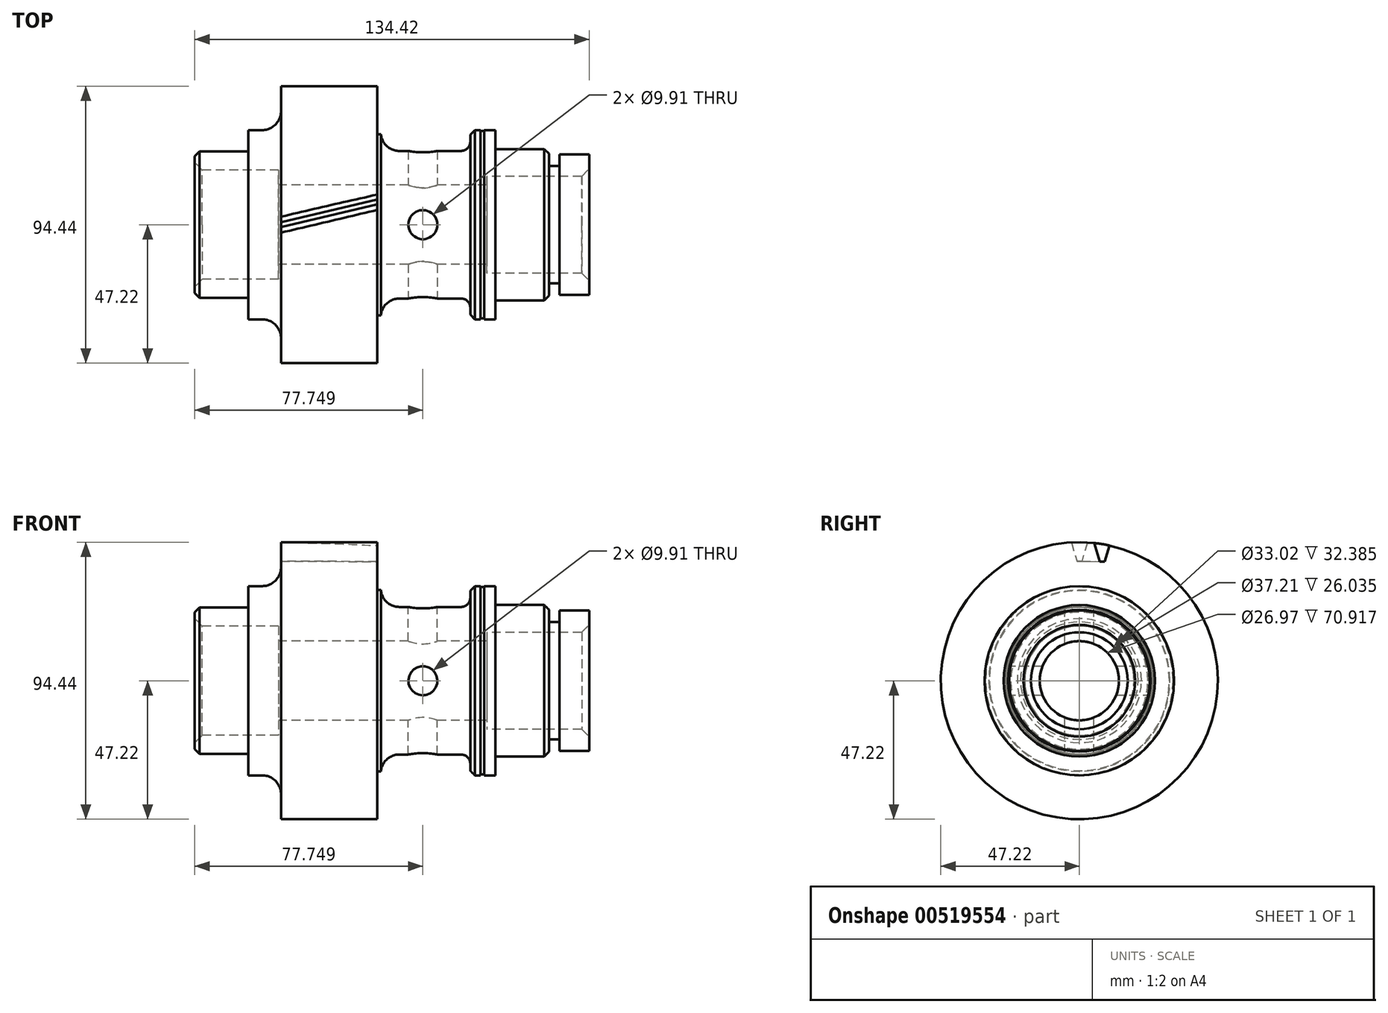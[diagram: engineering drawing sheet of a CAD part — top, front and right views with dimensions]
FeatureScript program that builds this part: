
annotation { "Feature Type Name" : "Feature", "Feature Type Description" : "" }
export const myFeature = defineFeature(function(context is Context, id is Id, definition is map)
    precondition{}
    {
        {
            var Q0;
            Q0=qCreatedBy(makeId("Front.planeOp"),FACE);
            var sketch = newSketch(context, id + "F0", { "sketchPlane" : qUnion([Q0])});
            skLineSegment(sketch, "E0", {"start": v(0, 0) * mm, "end": v(134.42, 0) * mm});
            skLineSegment(sketch, "E1", {"start": v(134.42, 0) * mm, "end": v(134.42, 23.94) * mm});
            skLineSegment(sketch, "E2", {"start": v(134.42, 23.94) * mm, "end": v(124.26, 23.94) * mm});
            skLineSegment(sketch, "E3", {"start": v(124.26, 23.94) * mm, "end": v(124.26, 20.02) * mm});
            skLineSegment(sketch, "E4", {"start": v(124.26, 20.02) * mm, "end": v(120.7, 20.02) * mm});
            skLineSegment(sketch, "E5", {"start": v(120.7, 20.02) * mm, "end": v(120.7, 25.8) * mm});
            skLineSegment(sketch, "E6", {"start": v(120.7, 25.8) * mm, "end": v(102.41, 25.8) * mm});
            skLineSegment(sketch, "E7", {"start": v(102.41, 25.8) * mm, "end": v(102.41, 32.26) * mm});
            skLineSegment(sketch, "E8", {"start": v(102.41, 32.26) * mm, "end": v(98.6, 32.26) * mm});
            skLineSegment(sketch, "E9", {"start": v(98.6, 32.26) * mm, "end": v(98.6, 31.94) * mm});
            skLineSegment(sketch, "E10", {"start": v(98.6, 31.94) * mm, "end": v(97.33, 31.94) * mm});
            skLineSegment(sketch, "E11", {"start": v(97.33, 31.94) * mm, "end": v(97.33, 32.26) * mm});
            skLineSegment(sketch, "E12", {"start": v(97.33, 32.26) * mm, "end": v(93.9, 32.26) * mm});
            skLineSegment(sketch, "E13", {"start": v(93.9, 32.26) * mm, "end": v(93.9, 25.15) * mm});
            skLineSegment(sketch, "E14", {"start": v(93.9, 25.15) * mm, "end": v(63.42, 25.15) * mm});
            skLineSegment(sketch, "E15", {"start": v(62.15, 47.22) * mm, "end": v(29.39, 47.22) * mm});
            skLineSegment(sketch, "E16", {"start": v(29.39, 47.22) * mm, "end": v(29.39, 32.26) * mm});
            skLineSegment(sketch, "E17", {"start": v(29.39, 32.26) * mm, "end": v(18.29, 32.26) * mm});
            skLineSegment(sketch, "E18", {"start": v(18.29, 24.92) * mm, "end": v(0, 24.92) * mm});
            skLineSegment(sketch, "E19", {"start": v(0, 24.92) * mm, "end": v(0, 0) * mm});
            skLineSegment(sketch, "E20", {"start": v(63.42, 25.15) * mm, "end": v(63.42, 30.87) * mm});
            skLineSegment(sketch, "E21", {"start": v(63.42, 30.87) * mm, "end": v(62.15, 30.87) * mm});
            skLineSegment(sketch, "E22", {"start": v(62.15, 30.87) * mm, "end": v(62.15, 47.22) * mm});
            skLineSegment(sketch, "E23", {"start": v(18.29, 24.92) * mm, "end": v(18.29, 32.26) * mm});
            skPoint(sketch, "E24.orphan", {"position": v(9.8, 32.26) * mm});
            skLineSegment(sketch, "E25", {"start": v(0, 18.6) * mm, "end": v(28.57, 18.6) * mm});
            skLineSegment(sketch, "E26", {"start": v(28.58, 18.6) * mm, "end": v(28.58, 13.49) * mm});
            skLineSegment(sketch, "E27", {"start": v(28.58, 13.49) * mm, "end": v(99.5, 13.49) * mm});
            skLineSegment(sketch, "E28", {"start": v(99.5, 13.49) * mm, "end": v(99.5, 16.51) * mm});
            skLineSegment(sketch, "E29", {"start": v(99.5, 16.51) * mm, "end": v(134.42, 16.51) * mm});
            skSolve(sketch);
        }
        {
            var Q0;
            {var subQ3=sQuery(id+"F0.wireOp",EDGE,"E2");Q0=makeQuery(id+"F0.imprint","IMPRINT",FACE,{"disambiguationData":[TD([[makeQuery(id+"F0.imprint","IMPRINT",EDGE,{"derivedFrom":subQ3}),1.0]])]});}
            var Q1;
            Q1=sQuery(id+"F0.wireOp",EDGE,"E0");
            revolve(context, id + "F1", {"entities" : qUnion([Q0]), "axis" : qUnion([Q1]), "revolveType" : RevolveType.FULL});
        }
        {
            var Q0;
            Q0=makeQuery(id+"F1.opRevolve","SWEPT_EDGE",EDGE,{"disambiguationData":[OSD([sQuery(id+"F0.wireOp",EDGE,"E14"),sQuery(id+"F0.wireOp",EDGE,"E20")])]});
            var Q1;
            Q1=makeQuery(id+"F1.opRevolve","SWEPT_EDGE",EDGE,{"disambiguationData":[OSD([sQuery(id+"F0.wireOp",EDGE,"E16"),sQuery(id+"F0.wireOp",EDGE,"E17")])]});
            fillet(context, id + "F2", {"entities" : qUnion([Q0, Q1]), "radius" : 6.35 * mm, "tangentPropagation" : true, "allowEdgeOverflow" : false});
        }
        {
            var Q0;
            Q0=makeQuery(id+"F1.opRevolve","SWEPT_EDGE",EDGE,{"disambiguationData":[OSD([sQuery(id+"F0.wireOp",EDGE,"E13"),sQuery(id+"F0.wireOp",EDGE,"E14")])]});
            fillet(context, id + "F3", {"entities" : qUnion([Q0]), "radius" : 3.17 * mm, "tangentPropagation" : true, "allowEdgeOverflow" : false});
        }
        {
            var Q0;
            Q0=makeQuery(id+"F1.opRevolve","SWEPT_EDGE",EDGE,{"disambiguationData":[OSD([sQuery(id+"F0.wireOp",EDGE,"E12"),sQuery(id+"F0.wireOp",EDGE,"E13")])]});
            var Q1;
            Q1=makeQuery(id+"F1.opRevolve","SWEPT_EDGE",EDGE,{"disambiguationData":[OSD([sQuery(id+"F0.wireOp",EDGE,"E5"),sQuery(id+"F0.wireOp",EDGE,"E6")])]});
            var Q2;
            Q2=makeQuery(id+"F1.opRevolve","SWEPT_EDGE",EDGE,{"disambiguationData":[OSD([sQuery(id+"F0.wireOp",EDGE,"E18"),sQuery(id+"F0.wireOp",EDGE,"E19")])]});
            chamfer(context, id + "F4", {"entities" : qUnion([Q0, Q1, Q2]), "width" : 1.57 * mm, "tangentPropagation" : true});
        }
        {
            var Q0;
            Q0=makeQuery(id+"F1.opRevolve","SWEPT_EDGE",EDGE,{"disambiguationData":[OSD([sQuery(id+"F0.wireOp",EDGE,"E19"),sQuery(id+"F0.wireOp",EDGE,"E25")])]});
            var Q1;
            Q1=makeQuery(id+"F1.opRevolve","SWEPT_EDGE",EDGE,{"disambiguationData":[OSD([sQuery(id+"F0.wireOp",EDGE,"E1"),sQuery(id+"F0.wireOp",EDGE,"E29")])]});
            chamfer(context, id + "F5", {"entities" : qUnion([Q0, Q1]), "width" : 2.54 * mm, "tangentPropagation" : true});
        }
        {
            var Q0;
            Q0=qCreatedBy(makeId("Top.planeOp"),FACE);
            var sketch = newSketch(context, id + "F6", { "sketchPlane" : qUnion([Q0])});
            skCircle(sketch, "E30", {"center": v(77.75, 0) * mm, "radius": 4.95 * mm});
            skSolve(sketch);
        }
        {
            var Q0;
            Q0=makeQuery(id+"F6.imprint","IMPRINT",FACE,{"disambiguationData":[TD([[makeQuery(id+"F6.imprint","IMPRINT",EDGE,{"derivedFrom":sQuery(id+"F6.wireOp",EDGE,"E30")}),1.0]])]});
            extrude(context, id + "F7", {"entities" : qUnion([Q0]), "operationType" : NewBodyOperationType.REMOVE, "endBound" : BoundingType.THROUGH_ALL, "oppositeDirection" : true, "depth" : 25.4 * mm, "hasSecondDirection" : true, "secondDirectionBound" : SecondDirectionBoundingType.THROUGH_ALL, "secondDirectionOppositeDirection" : false, "secondDirectionDepth" : 25.4 * mm});
        }
        {
            var Q0;
            Q0=qCreatedBy(makeId("Front.planeOp"),FACE);
            var sketch = newSketch(context, id + "F8", { "sketchPlane" : qUnion([Q0])});
            skCircle(sketch, "E31", {"center": v(77.75, 0) * mm, "radius": 4.95 * mm});
            skSolve(sketch);
        }
        {
            var Q0;
            Q0=qSketchRegion(id+"F8",true);
            extrude(context, id + "F9", {"entities" : qUnion([Q0]), "operationType" : NewBodyOperationType.REMOVE, "endBound" : BoundingType.THROUGH_ALL, "oppositeDirection" : true, "depth" : 25.4 * mm, "hasSecondDirection" : true, "secondDirectionBound" : SecondDirectionBoundingType.THROUGH_ALL, "secondDirectionOppositeDirection" : false, "secondDirectionDepth" : 25.4 * mm});
        }
        {
            var Q0;
            Q0=makeQuery(id+"F1.opRevolve","SWEPT_FACE",FACE,{"disambiguationData":[OSD([sQuery(id+"F0.wireOp",EDGE,"E16")])]});
            var sketch = newSketch(context, id + "F10", { "sketchPlane" : qUnion([Q0])});
            skLineSegment(sketch, "E32", {"start": v(0, 0) * mm, "end": v(0, 55.57) * mm, "construction": true});
            skCircle(sketch, "E33", {"center": v(0, 0) * mm, "radius": 40.77 * mm});
            skLineSegment(sketch, "E34.0", {"start": v(0.83, 0) * mm, "end": v(0.83, 55.57) * mm, "construction": true});
            skLineSegment(sketch, "E35.0", {"start": v(2.73, 0) * mm, "end": v(2.73, 55.57) * mm, "construction": true});
            skLineSegment(sketch, "E36", {"start": v(3.26, 48.9) * mm, "end": v(0.83, 40.76) * mm});
            skLineSegment(sketch, "E37.MirrorCS", {"start": v(-3.26, 48.9) * mm, "end": v(-0.83, 40.76) * mm});
            skPoint(sketch, "E38", {"position": v(2.73, 47.14) * mm});
            skCircle(sketch, "E39", {"center": v(0, 0) * mm, "radius": 49.02 * mm});
            skPoint(sketch, "E40.orphan", {"position": v(-2.73, 47.14) * mm});
            skLineSegment(sketch, "E41", {"start": v(-0.83, 40.76) * mm, "end": v(0.83, 40.76) * mm});
            skSolve(sketch);
        }
        {
            var Q0;
            Q0=makeQuery(id+"F1.opRevolve","SWEPT_FACE",FACE,{"disambiguationData":[OSD([sQuery(id+"F0.wireOp",EDGE,"E22")])]});
            var sketch = newSketch(context, id + "F11", { "sketchPlane" : qUnion([Q0])});
            skLineSegment(sketch, "E42", {"start": v(0, 0) * mm, "end": v(0, 55.65) * mm});
            skLineSegment(sketch, "E43", {"start": v(0, 0) * mm, "end": v(9.23, 55.33) * mm, "construction": true});
            skLineSegment(sketch, "E44.0", {"start": v(-0.83, 0.14) * mm, "end": v(8.4, 55.47) * mm, "construction": true});
            skLineSegment(sketch, "E45.0", {"start": v(-2.7, 0.45) * mm, "end": v(6.53, 55.78) * mm, "construction": true});
            skCircle(sketch, "E46", {"center": v(0, 0) * mm, "radius": 40.7 * mm});
            skLineSegment(sketch, "E47", {"start": v(5.87, 40.28) * mm, "end": v(5.05, 46.95) * mm});
            skLineSegment(sketch, "E48.MirrorCS", {"start": v(7.53, 40) * mm, "end": v(10.46, 46.04) * mm});
            skLineSegment(sketch, "E49", {"start": v(5.87, 40.28) * mm, "end": v(7.53, 40) * mm});
            skSolve(sketch);
        }
        {
            var Q0;
            Q0=sQuery(id+"F10.wireOp",VERTEX,"E38");
            var Q1;
            Q1=sQuery(id+"F11.wireOp",VERTEX,"E47.end");
            var Q2;
            Q2=sQuery(id+"F10.wireOp",VERTEX,"E40.orphan");
            cPlane(context, id + "F12", {"entities" : qUnion([Q0, Q1, Q2]), "cplaneType" : CPlaneType.THREE_POINT, "offset" : 25.4 * mm, "width" : 152.4 * mm, "height" : 152.4 * mm});
        }
        {
            var Q0;
            Q0=qCreatedBy(id+"F12.planeOp",FACE);
            var sketch = newSketch(context, id + "F13", { "sketchPlane" : qUnion([Q0])});
            skPoint(sketch, "E50.0", {"position": v(29.11, 2.73) * mm});
            skPoint(sketch, "E51.0", {"position": v(61.88, -5.05) * mm});
            skLineSegment(sketch, "E52", {"start": v(29.11, 2.73) * mm, "end": v(61.88, -5.05) * mm});
            skSolve(sketch);
        }
        {
            var Q0;
            {var subQ0=sQuery(id+"F10.wireOp",EDGE,"E41");var subQ1=sQuery(id+"F10.wireOp",EDGE,"E36");var subQ2=sQuery(id+"F10.wireOp",EDGE,"E33");var subQ3=makeQuery(id+"F10.imprint","INTERSECT",VERTEX,{"derivedFrom":[subQ2,subQ1,subQ0]});Q0=makeQuery(id+"F10.imprint","IMPRINT",FACE,{"disambiguationData":[TD([[makeQuery(id+"F10.imprint","IMPRINT",EDGE,{"disambiguationData":[TD([[subQ3,-1.0]])],"derivedFrom":subQ2}),-1.0]])]});}
            var Q1;
            {var subQ0=sQuery(id+"F10.wireOp",EDGE,"E39");var subQ1=sQuery(id+"F10.wireOp",EDGE,"E36");var subQ2=makeQuery(id+"F10.imprint","INTERSECT",VERTEX,{"derivedFrom":[subQ1,subQ0]});Q1=makeQuery(id+"F10.imprint","IMPRINT",FACE,{"disambiguationData":[TD([[makeQuery(id+"F10.imprint","IMPRINT",EDGE,{"disambiguationData":[TD([[subQ2,-1.0]])],"derivedFrom":subQ0}),1.0]])]});}
            var Q2;
            Q2=sQuery(id+"F13.wireOp",EDGE,"E52");
            sweep(context, id + "F14", {"operationType" : NewBodyOperationType.REMOVE, "profiles" : qUnion([Q0, Q1]), "path" : qUnion([Q2])});
        }
    });
